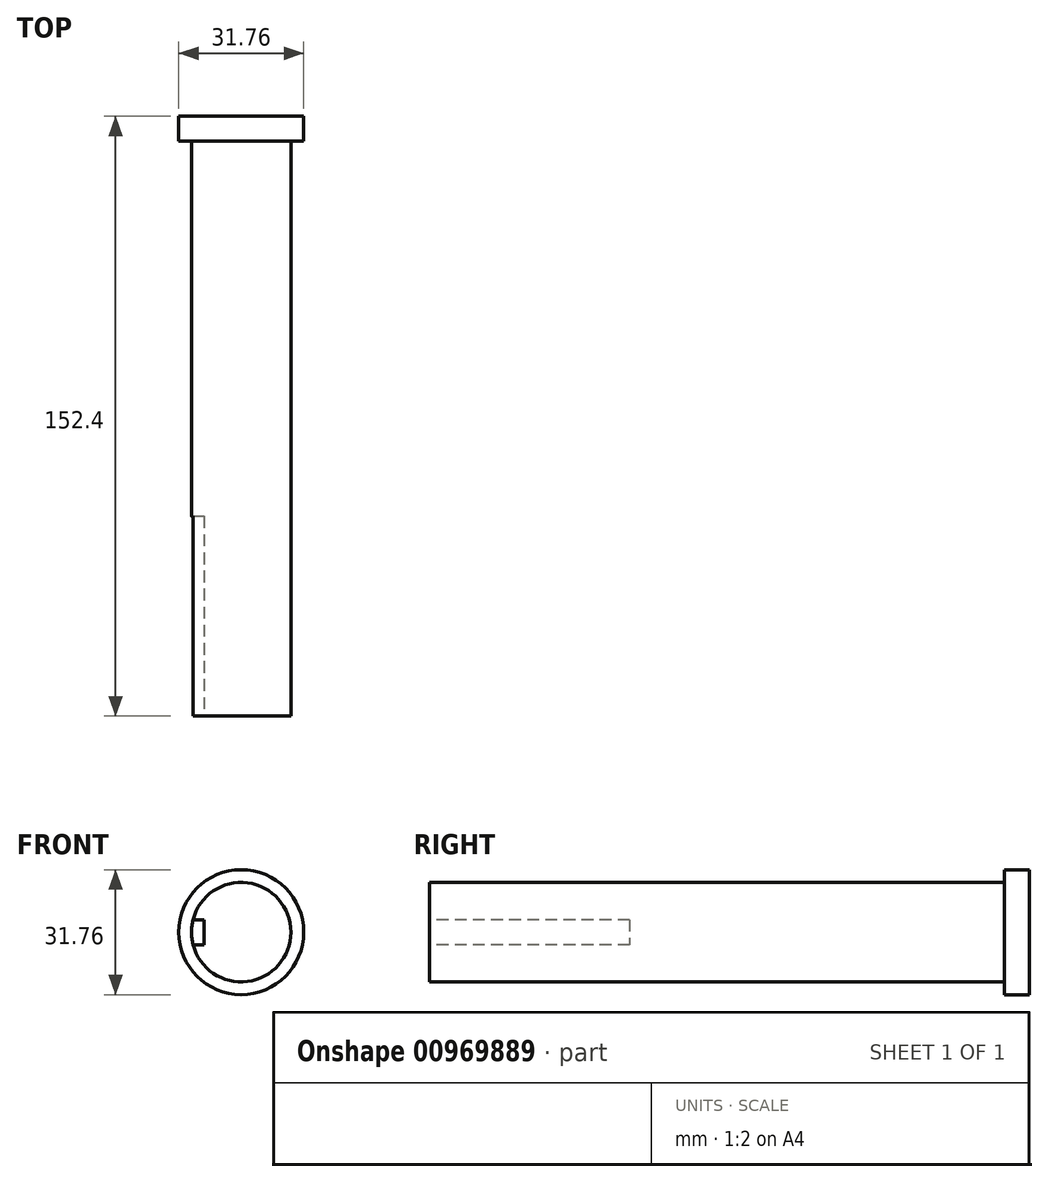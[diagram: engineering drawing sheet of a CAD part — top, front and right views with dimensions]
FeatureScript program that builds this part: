
annotation { "Feature Type Name" : "Feature", "Feature Type Description" : "" }
export const myFeature = defineFeature(function(context is Context, id is Id, definition is map)
    precondition{}
    {
        {
            var Q0;
            Q0=qCreatedBy(makeId("Front.planeOp"),FACE);
            var sketch = newSketch(context, id + "F0", { "sketchPlane" : qUnion([Q0])});
            skCircle(sketch, "E0", {"center": v(0, 0) * mm, "radius": 15.88 * mm});
            skCircle(sketch, "E1", {"center": v(0, 0) * mm, "radius": 12.64 * mm});
            skSolve(sketch);
        }
        {
            var Q0;
            Q0=makeQuery(id+"F0.imprint","IMPRINT",FACE,{"disambiguationData":[TD([[makeQuery(id+"F0.imprint","IMPRINT",EDGE,{"derivedFrom":sQuery(id+"F0.wireOp",EDGE,"E0")}),1.0]])]});
            extrude(context, id + "F1", {"entities" : qUnion([Q0]), "depth" : 6.35 * mm, "offsetDistance" : 25.4 * mm});
        }
        {
            var Q0;
            Q0=qCreatedBy(makeId("Front.planeOp"),FACE);
            var sketch = newSketch(context, id + "F2", { "sketchPlane" : qUnion([Q0])});
            skCircle(sketch, "E2", {"center": v(0, 0) * mm, "radius": 12.64 * mm});
            skSolve(sketch);
        }
        {
            var Q0;
            Q0 = qSketchRegion(id + "F2", true);
            extrude(context, id + "F3", {"entities" : qUnion([Q0]), "operationType" : NewBodyOperationType.ADD, "depth" : 152.4 * mm, "offsetDistance" : 25.4 * mm});
        }
        {
            var Q0;
            Q0=makeQuery(id+"F3.opExtrude","CAP_FACE",FACE,{"disambiguationData":[OSD([sQuery(id+"F2.wireOp",EDGE,"E2")])],"isStart":false});
            var sketch = newSketch(context, id + "F4", { "sketchPlane" : qUnion([Q0])});
            skLineSegment(sketch, "E3.bottom", {"start": v(-12.64, 3.18) * mm, "end": v(-9.46, 3.18) * mm});
            skLineSegment(sketch, "E3.top", {"start": v(-12.64, -3.18) * mm, "end": v(-9.46, -3.18) * mm});
            skLineSegment(sketch, "E3.left", {"start": v(-12.64, 3.18) * mm, "end": v(-12.64, -3.18) * mm});
            skLineSegment(sketch, "E3.right", {"start": v(-9.46, 3.18) * mm, "end": v(-9.46, -3.18) * mm});
            skPoint(sketch, "E3.middle", {"position": v(-11.05, 0) * mm});
            skPoint(sketch, "E4.end.orphan", {"position": v(-12.64, 0) * mm});
            skSolve(sketch);
        }
        {
            var Q0;
            {var subQ4=sQuery(id+"F4.wireOp",EDGE,"E3.right");Q0=makeQuery(id+"F4.imprint","IMPRINT",FACE,{"disambiguationData":[TD([[makeQuery(id+"F4.imprint","IMPRINT",EDGE,{"derivedFrom":subQ4}),-1.0]])]});}
            extrude(context, id + "F5", {"entities" : qUnion([Q0]), "operationType" : NewBodyOperationType.REMOVE, "oppositeDirection" : true, "depth" : 50.8 * mm, "offsetDistance" : 25.4 * mm});
        }
    });
